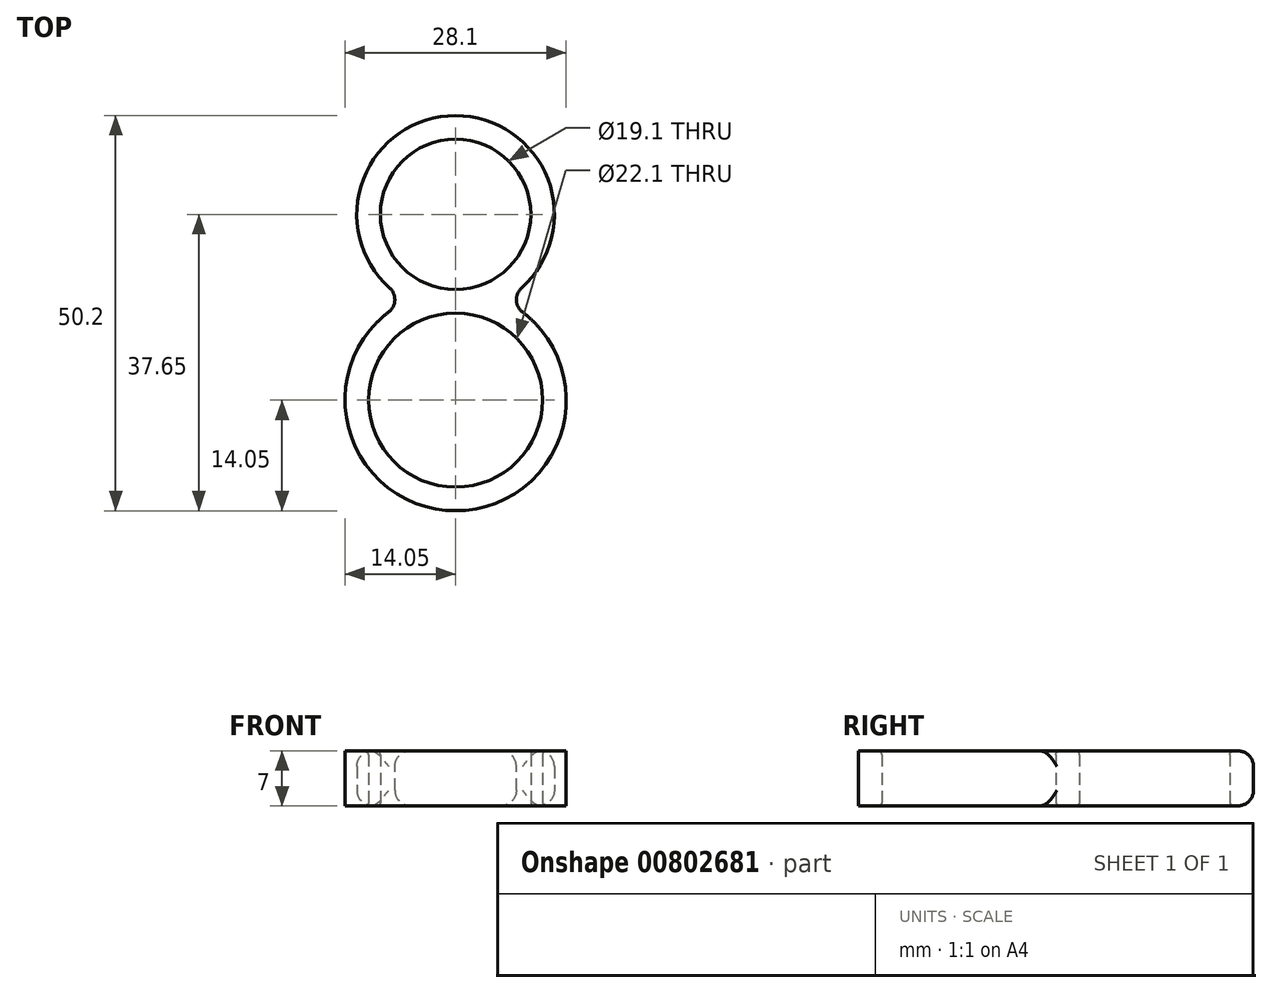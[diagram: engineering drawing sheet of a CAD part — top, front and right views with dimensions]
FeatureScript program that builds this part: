
annotation { "Feature Type Name" : "Feature", "Feature Type Description" : "" }
export const myFeature = defineFeature(function(context is Context, id is Id, definition is map)
    precondition{}
    {
        {
            var Q0;
            Q0=qCreatedBy(makeId("Top.planeOp"),FACE);
            var sketch = newSketch(context, id + "F0", { "sketchPlane" : qUnion([Q0])});
            skCircle(sketch, "E0", {"center": v(0, 0) * mm, "radius": 11.05 * mm});
            skCircle(sketch, "E1", {"center": v(0, 23.6) * mm, "radius": 9.55 * mm});
            skCircle(sketch, "E2", {"center": v(0, 23.6) * mm, "radius": 12.55 * mm});
            skCircle(sketch, "E3", {"center": v(0, 0) * mm, "radius": 14.05 * mm});
            skSolve(sketch);
        }
        {
            var Q0;
            {var subQ0=sQuery(id+"F0.wireOp",EDGE,"E1");Q0=makeQuery(id+"F0.imprint","IMPRINT",FACE,{"disambiguationData":[TD([[makeQuery(id+"F0.imprint","IMPRINT",EDGE,{"derivedFrom":subQ0}),-1.0]])]});}
            var Q1;
            {var subQ0=sQuery(id+"F0.wireOp",EDGE,"E0");Q1=makeQuery(id+"F0.imprint","IMPRINT",FACE,{"disambiguationData":[TD([[makeQuery(id+"F0.imprint","IMPRINT",EDGE,{"derivedFrom":subQ0}),-1.0]])]});}
            var Q2;
            {var subQ0=sQuery(id+"F0.wireOp",EDGE,"E2");var subQ1=makeQuery(id+"F0.imprint","INTERSECT",VERTEX,{"derivedFrom":[sQuery(id+"F0.wireOp",EDGE,"E0"),subQ0]});Q2=makeQuery(id+"F0.imprint","IMPRINT",FACE,{"disambiguationData":[TD([[makeQuery(id+"F0.imprint","IMPRINT",EDGE,{"disambiguationData":[TD([[subQ1,1.0]])],"derivedFrom":subQ0}),1.0]])]});}
            extrude(context, id + "F1", {"entities" : qUnion([Q0, Q1, Q2]), "depth" : 7 * mm, "offsetDistance" : 25 * mm});
        }
        {
            var Q0;
            Q0=makeQuery(id+"F1.opExtrude","SWEPT_FACE",FACE,{"disambiguationData":[OSD([sQuery(id+"F0.wireOp",EDGE,"E0")])]});
            var Q1;
            Q1=makeQuery(id+"F1.opExtrude","SWEPT_FACE",FACE,{"disambiguationData":[OSD([sQuery(id+"F0.wireOp",EDGE,"E1")])]});
            fillet(context, id + "F2", {"entities" : qUnion([Q0, Q1]), "radius" : .5 * mm, "tangentPropagation" : true, "allowEdgeOverflow" : false});
        }
        {
            var Q0;
            Q0=makeQuery(id+"F1.opExtrude","SWEPT_FACE",FACE,{"disambiguationData":[OSD([sQuery(id+"F0.wireOp",EDGE,"E2")])]});
            fillet(context, id + "F3", {"entities" : qUnion([Q0]), "radius" : 2 * mm, "tangentPropagation" : true, "allowEdgeOverflow" : false});
        }
    });
